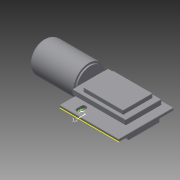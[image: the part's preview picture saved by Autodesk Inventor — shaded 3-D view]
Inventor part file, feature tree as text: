
AUTODESK INVENTOR PART (.ipt)
format: ipt  version: 2016 (Build 200138000, 138)  size: 230,400 bytes
history: native  units: in
note: dims shown in document units (in); Inventor stores cm internally (conversion verified against a paired STEP export)
features: extrude x7, sketch x7, fillet x2
ambient origin geometry x8: Origin, YZ Plane, XZ Plane, XY Plane, X Axis, Y Axis, Z Axis, Center Point
bodies: Solid1 (feature_tree)
feature tree (16):
  extrude  "Extrusion1"  Depth=0.9843in
  extrude  "Extrusion2"  Depth=0.6535in
  extrude  "Extrusion3"  Depth=0.1102in
  extrude  "Extrusion4"  Depth=0.1417in TaperAngle=0.0deg
  extrude  "Extrusion5"  Depth=0.0945in
  fillet  "Fillet1"  Radius=0.0512in
  extrude  "Extrusion6"  Depth=0.0787in TaperAngle=0.0deg
  extrude  "Extrusion7"  Depth=0.0079in TaperAngle=0.0deg
  fillet  "Fillet2"  Radius=0.5118in
  sketch  "Sketch1"  dims[d0=0.9055in d1=0.9843in]
  sketch  "Sketch2"  dims[d2=0.0394in d3=0.0in d4=0.6535in]
  sketch  "Sketch3"  dims[d5=0.4882in d6=0.1102in]
  sketch  "Sketch4"  dims[d7=0.2362in d8=0.1417in d9=0.0in]
  sketch  "Sketch6"  dims[d11=0.0512in d12=0.0945in d13=0.0512in]
  sketch  "Sketch7"  dims[d14=0.1339in d15=0.0787in d16=0.0in]
  sketch  "Sketch8"  dims[d17=0.4488in d18=0.7874in d19=0.0in d20=0.5118in d21=0.7638in d22=0.0in d23=0.0984in d24=0.6299in d25=0.5118in d26=0.0512in d27=0.1811in d28=0.1102in d29=0.0in d37=0.1102in d38=0.0in d39=0.0079in]
